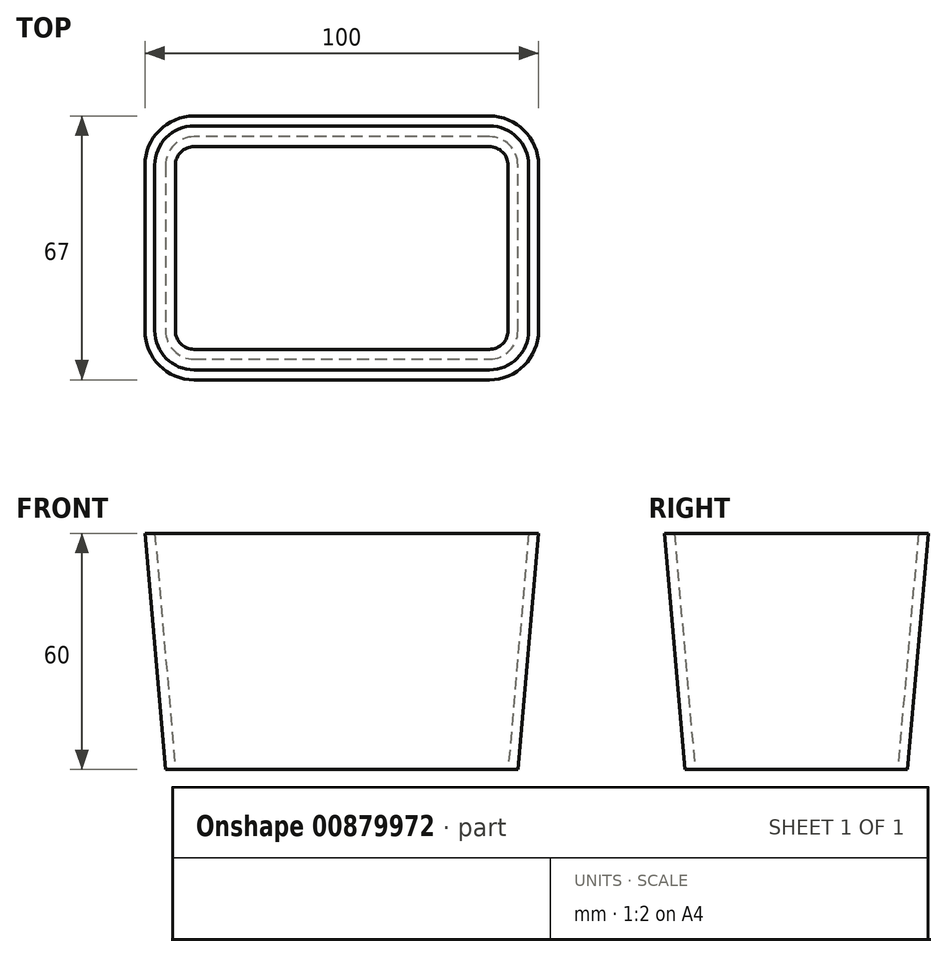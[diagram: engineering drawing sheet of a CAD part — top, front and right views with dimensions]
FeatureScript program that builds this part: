
annotation { "Feature Type Name" : "Feature", "Feature Type Description" : "" }
export const myFeature = defineFeature(function(context is Context, id is Id, definition is map)
    precondition{}
    {
        {
            var Q0;
            Q0=qCreatedBy(makeId("Top.planeOp"),FACE);
            var sketch = newSketch(context, id + "F0", { "sketchPlane" : qUnion([Q0])});
            skPoint(sketch, "E0.middle", {"position": v(0, 0) * mm});
            skArc(sketch, "E1", {"start": v(-37.5, 31) * mm, "mid": v(-44.57, 28.07) * mm, "end": v(-47.5, 21) * mm});
            skArc(sketch, "E2", {"start": v(47.5, 21) * mm, "mid": v(44.57, 28.07) * mm, "end": v(37.5, 31) * mm});
            skArc(sketch, "E3", {"start": v(37.5, -31) * mm, "mid": v(44.57, -28.07) * mm, "end": v(47.5, -21) * mm});
            skArc(sketch, "E4", {"start": v(-47.5, -21) * mm, "mid": v(-44.57, -28.07) * mm, "end": v(-37.5, -31) * mm});
            skLineSegment(sketch, "E5.bottom", {"start": v(37.5, 31) * mm, "end": v(-37.5, 31) * mm});
            skLineSegment(sketch, "E5.top", {"start": v(37.5, -31) * mm, "end": v(-37.5, -31) * mm});
            skLineSegment(sketch, "E5.left", {"start": v(47.5, 21) * mm, "end": v(47.5, -21) * mm});
            skLineSegment(sketch, "E5.right", {"start": v(-47.5, 21) * mm, "end": v(-47.5, -21) * mm});
            skSolve(sketch);
        }
        {
            var Q0;
            Q0=qCreatedBy(makeId("Front.planeOp"),FACE);
            var sketch = newSketch(context, id + "F1", { "sketchPlane" : qUnion([Q0])});
            skLineSegment(sketch, "E6.bottom", {"start": v(-42.25, -60) * mm, "end": v(-44.75, -60) * mm});
            skPoint(sketch, "E6.middle", {"position": v(0, 0) * mm});
            skLineSegment(sketch, "E7", {"start": v(-47.5, 0) * mm, "end": v(-50, 0) * mm});
            skLineSegment(sketch, "E8", {"start": v(-47.5, 0) * mm, "end": v(-42.25, -60) * mm});
            skLineSegment(sketch, "E9", {"start": v(-50, 0) * mm, "end": v(-44.75, -60) * mm});
            skPoint(sketch, "E10.start.orphan", {"position": v(1.4, 0) * mm});
            skSolve(sketch);
        }
        {
            var Q0;
            Q0=makeQuery(id+"F1.imprint","IMPRINT",FACE,{"disambiguationData":[TD([[makeQuery(id+"F1.imprint","IMPRINT",EDGE,{"derivedFrom":sQuery(id+"F1.wireOp",EDGE,"E6.bottom")}),-1.0]])]});
            var Q1;
            Q1=sQuery(id+"F0.wireOp",EDGE,"E5.right");
            var Q2;
            Q2=sQuery(id+"F0.wireOp",EDGE,"E4");
            var Q3;
            Q3=sQuery(id+"F0.wireOp",EDGE,"E5.top");
            var Q4;
            Q4=sQuery(id+"F0.wireOp",EDGE,"E3");
            var Q5;
            Q5=sQuery(id+"F0.wireOp",EDGE,"E5.left");
            var Q6;
            Q6=sQuery(id+"F0.wireOp",EDGE,"E2");
            var Q7;
            Q7=sQuery(id+"F0.wireOp",EDGE,"E5.bottom");
            var Q8;
            Q8=sQuery(id+"F0.wireOp",EDGE,"E1");
            sweep(context, id + "F2", {"profiles" : qUnion([Q0]), "path" : qUnion([Q1, Q2, Q3, Q4, Q5, Q6, Q7, Q8])});
        }
    });
